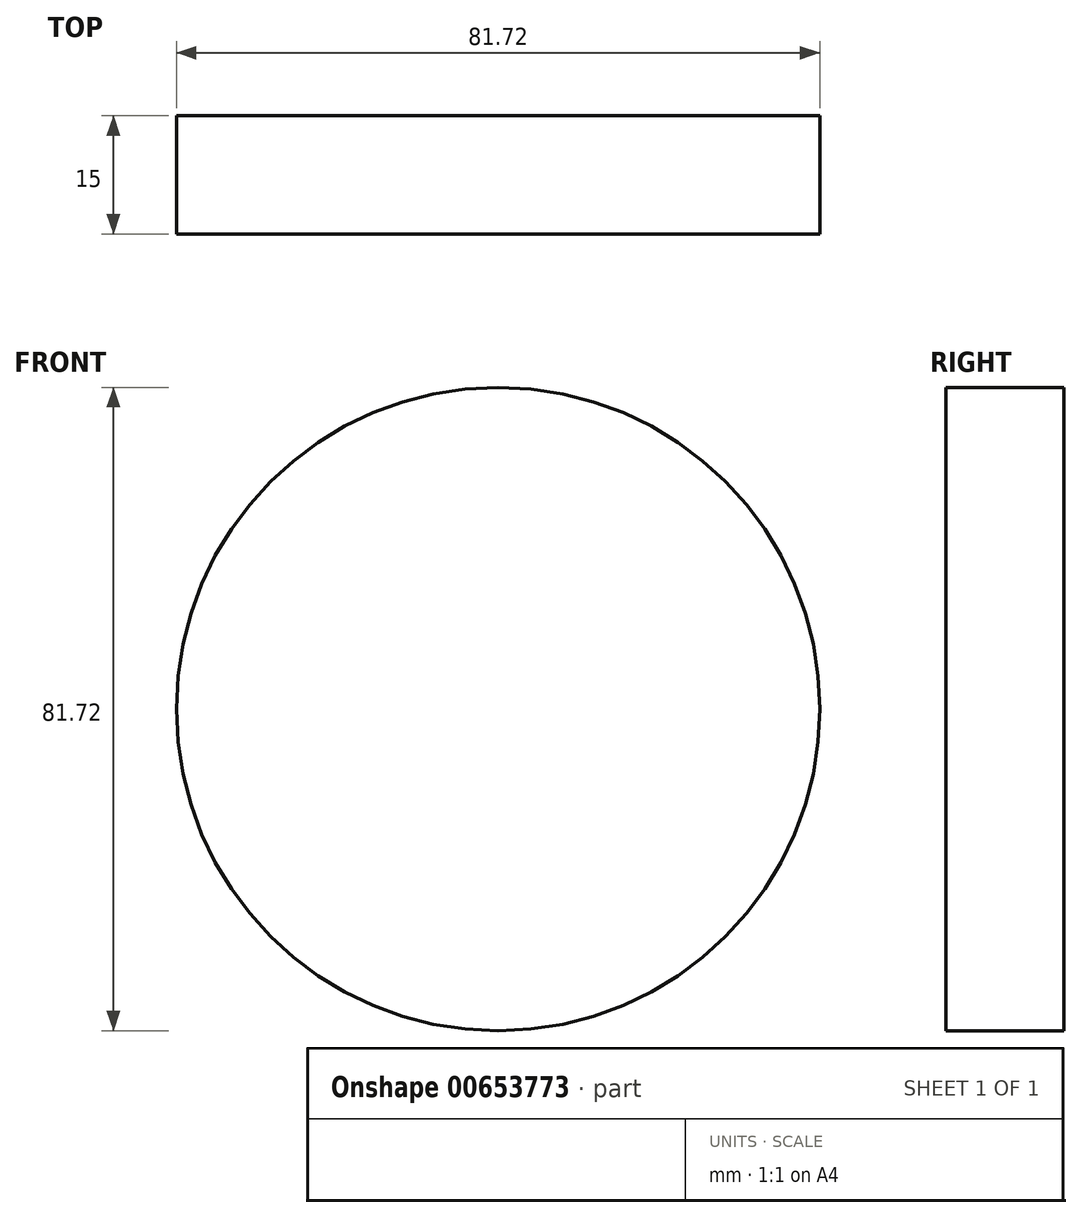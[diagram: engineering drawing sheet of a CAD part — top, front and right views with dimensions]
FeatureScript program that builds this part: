
annotation { "Feature Type Name" : "Feature", "Feature Type Description" : "" }
export const myFeature = defineFeature(function(context is Context, id is Id, definition is map)
    precondition{}
    {
        {
            var Q0;
            Q0=qCreatedBy(makeId("Front.planeOp"),FACE);
            var sketch = newSketch(context, id + "F0", { "sketchPlane" : qUnion([Q0])});
            skCircle(sketch, "E0", {"center": v(0, 0) * mm, "radius": 40.86 * mm});
            skSolve(sketch);
        }
        {
            var Q0;
            Q0=makeQuery(id+"F0.imprint","IMPRINT",FACE,{"disambiguationData":[TD([[makeQuery(id+"F0.imprint","IMPRINT",EDGE,{"derivedFrom":sQuery(id+"F0.wireOp",EDGE,"E0")}),1.0]])]});
            extrude(context, id + "F1", {"entities" : qUnion([Q0]), "depth" : 15 * mm, "offsetDistance" : 25 * mm});
        }
        {
            var Q0;
            Q0=makeQuery(id+"F1.opExtrude","CAP_FACE",FACE,{"disambiguationData":[OSD([sQuery(id+"F0.wireOp",EDGE,"E0")])],"isStart":false});
            var sketch = newSketch(context, id + "F2", { "sketchPlane" : qUnion([Q0])});
            skCircle(sketch, "E1", {"center": v(-47.58, -30.63) * mm, "radius": 39.32 * mm});
            skSolve(sketch);
        }
        {
            var Q0;
            {var subQ0=sQuery(id+"F2.wireOp",EDGE,"E1");var subQ1=makeQuery(id+"F1.opExtrude","CAP_EDGE",EDGE,{"disambiguationData":[OSD([sQuery(id+"F0.wireOp",EDGE,"E0")])],"isStart":false});var subQ2=makeQuery(id+"F2.imprint","INTERSECT",VERTEX,{"disambiguationData":[OD(0.0)],"derivedFrom":[subQ1,subQ0]});Q0=makeQuery(id+"F2.imprint","IMPRINT",FACE,{"disambiguationData":[TD([[makeQuery(id+"F2.imprint","IMPRINT",EDGE,{"disambiguationData":[TD([[subQ2,-1.0]])],"derivedFrom":subQ0}),1.0]])]});}
            extrude(context, id + "F3", {"entities" : qUnion([Q0]), "operationType" : NewBodyOperationType.REMOVE, "oppositeDirection" : true, "depth" : 25 * mm, "offsetDistance" : 25 * mm});
        }
    });
